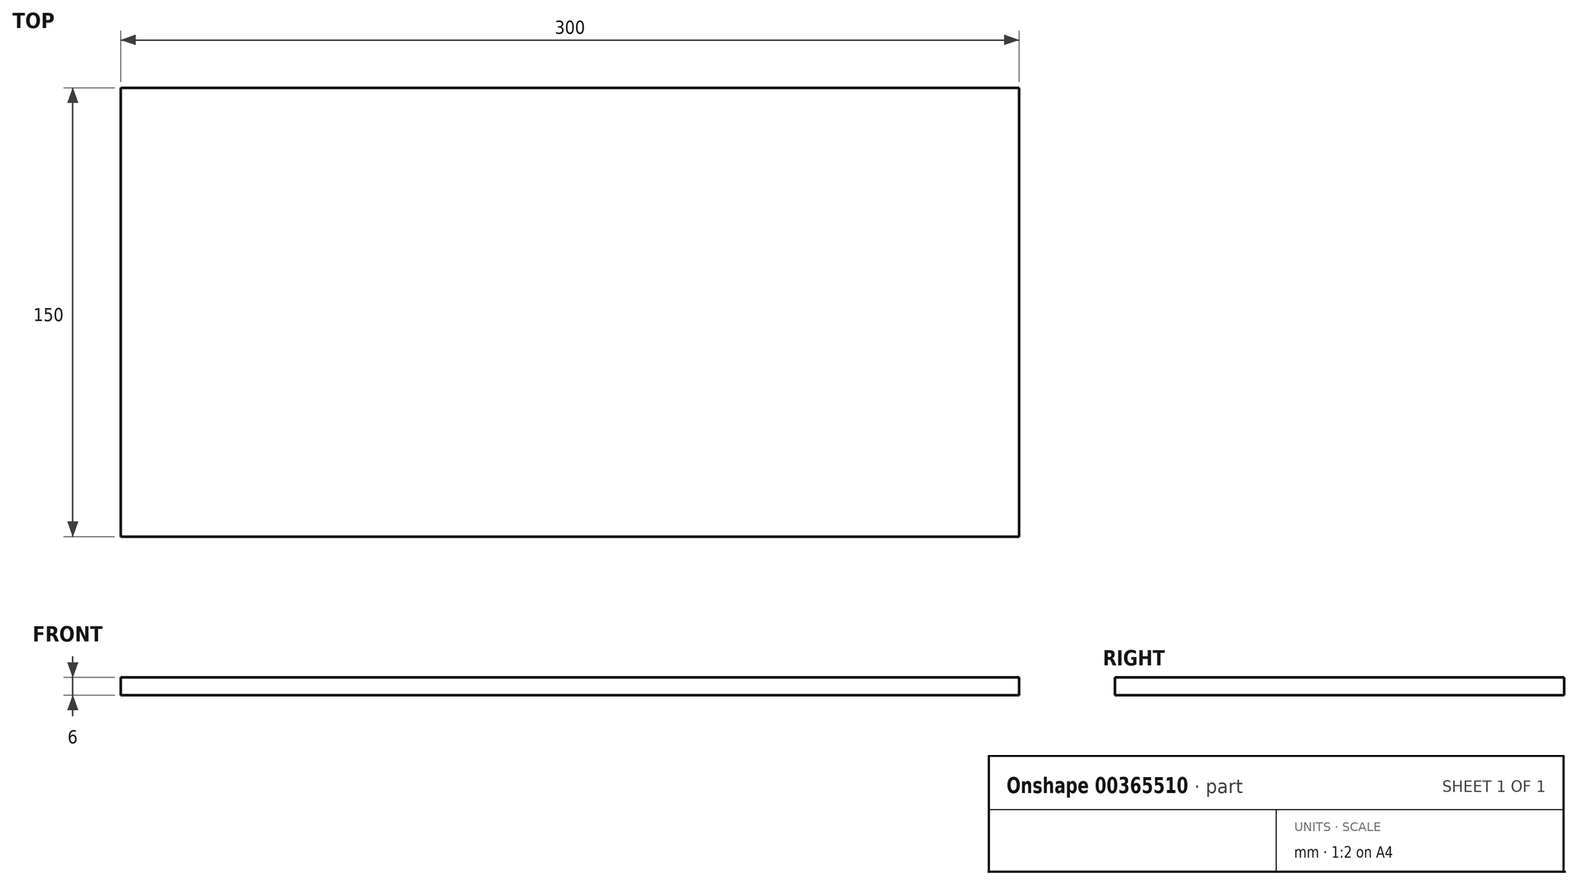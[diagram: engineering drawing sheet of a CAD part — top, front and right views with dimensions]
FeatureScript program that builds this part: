
annotation { "Feature Type Name" : "Feature", "Feature Type Description" : "" }
export const myFeature = defineFeature(function(context is Context, id is Id, definition is map)
    precondition{}
    {
        {
            var Q0;
            Q0=qCreatedBy(makeId("Top.planeOp"),FACE);
            var sketch = newSketch(context, id + "F0", { "sketchPlane" : qUnion([Q0])});
            skLineSegment(sketch, "E0.bottom", {"start": v(-150, -75) * mm, "end": v(150, -75) * mm});
            skLineSegment(sketch, "E0.top", {"start": v(-150, 75) * mm, "end": v(150, 75) * mm});
            skLineSegment(sketch, "E0.left", {"start": v(-150, -75) * mm, "end": v(-150, 75) * mm});
            skLineSegment(sketch, "E0.right", {"start": v(150, -75) * mm, "end": v(150, 75) * mm});
            skPoint(sketch, "E0.middle", {"position": v(0, 0) * mm});
            skSolve(sketch);
        }
        {
            var Q0;
            Q0=makeQuery(id+"F0.imprint","IMPRINT",FACE,{"disambiguationData":[TD([[makeQuery(id+"F0.imprint","IMPRINT",EDGE,{"derivedFrom":sQuery(id+"F0.wireOp",EDGE,"E0.bottom")}),1.0]])]});
            extrude(context, id + "F1", {"entities" : qUnion([Q0]), "depth" : 6 * mm});
        }
    });
